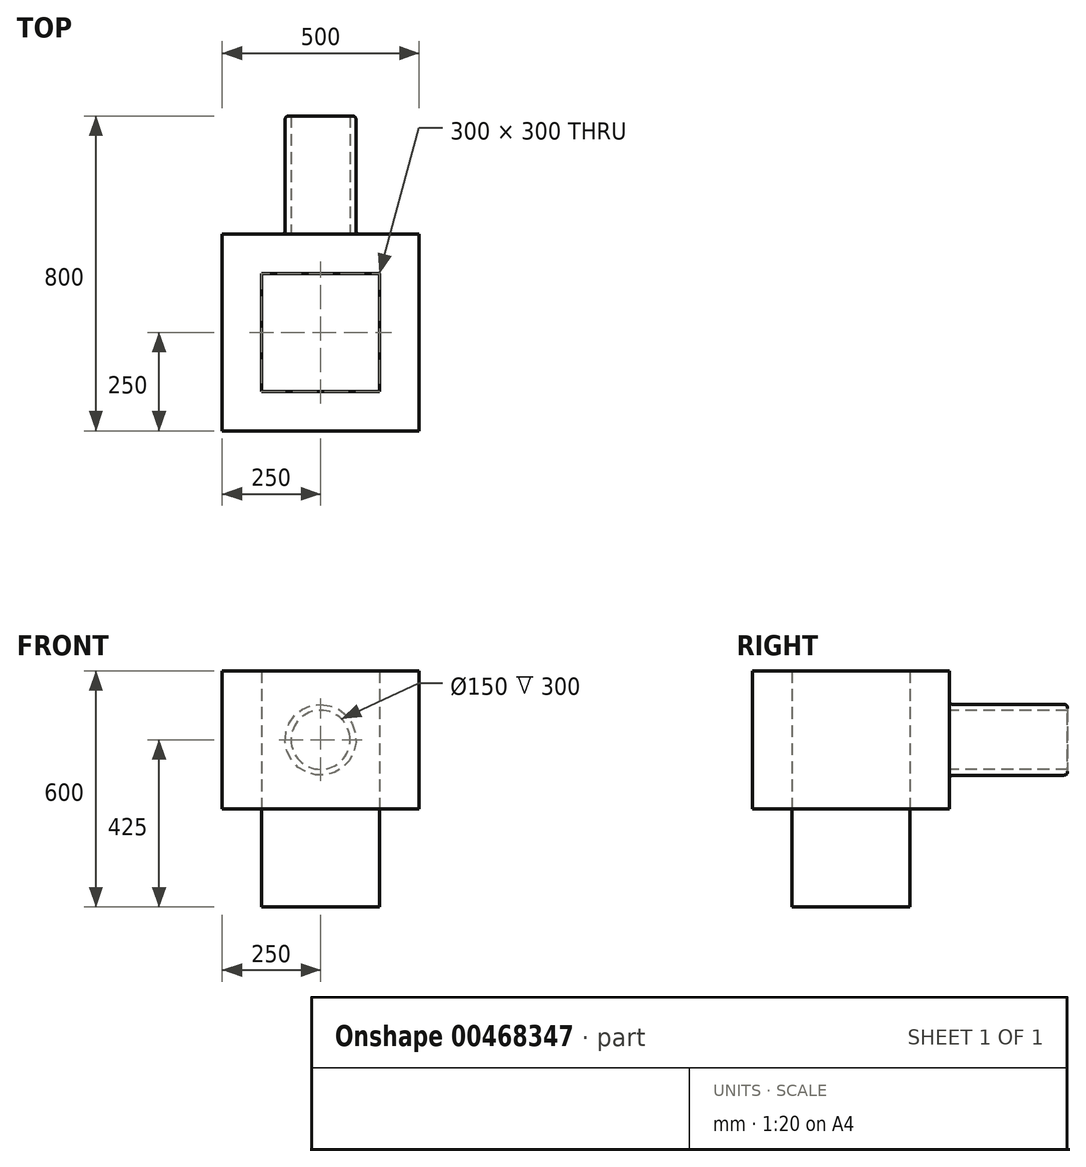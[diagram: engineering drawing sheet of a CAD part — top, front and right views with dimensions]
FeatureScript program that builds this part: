
annotation { "Feature Type Name" : "Feature", "Feature Type Description" : "" }
export const myFeature = defineFeature(function(context is Context, id is Id, definition is map)
    precondition{}
    {
        {
            var Q0;
            Q0=qCreatedBy(makeId("Top.planeOp"),FACE);
            var sketch = newSketch(context, id + "F0", { "sketchPlane" : qUnion([Q0])});
            skLineSegment(sketch, "E0", {"start": v(0, 0) * mm, "end": v(0, 500) * mm});
            skLineSegment(sketch, "E1", {"start": v(0, 500) * mm, "end": v(500, 500) * mm});
            skLineSegment(sketch, "E2", {"start": v(500, 500) * mm, "end": v(500, 0) * mm});
            skLineSegment(sketch, "E3", {"start": v(500, 0) * mm, "end": v(0, 0) * mm});
            skLineSegment(sketch, "E4.0", {"start": v(100, 100) * mm, "end": v(100, 400) * mm});
            skLineSegment(sketch, "E5.0", {"start": v(100, 400) * mm, "end": v(400, 400) * mm});
            skLineSegment(sketch, "E6.0", {"start": v(400, 100) * mm, "end": v(100, 100) * mm});
            skLineSegment(sketch, "E7.0", {"start": v(400, 400) * mm, "end": v(400, 100) * mm});
            skSolve(sketch);
        }
        {
            var Q0;
            Q0=makeQuery(id+"F0.imprint","IMPRINT",FACE,{"disambiguationData":[TD([[makeQuery(id+"F0.imprint","IMPRINT",EDGE,{"derivedFrom":sQuery(id+"F0.wireOp",EDGE,"E0")}),-1.0]])]});
            extrude(context, id + "F1", {"entities" : qUnion([Q0]), "depth" : 350 * mm, "offsetDistance" : 25 * mm});
        }
        {
            var Q0;
            Q0=makeQuery(id+"F1.opExtrude","CAP_FACE",FACE,{"disambiguationData":[OSD([sQuery(id+"F0.wireOp",EDGE,"E0"),sQuery(id+"F0.wireOp",EDGE,"E1"),sQuery(id+"F0.wireOp",EDGE,"E2"),sQuery(id+"F0.wireOp",EDGE,"E3"),sQuery(id+"F0.wireOp",EDGE,"E4.0"),sQuery(id+"F0.wireOp",EDGE,"E5.0"),sQuery(id+"F0.wireOp",EDGE,"E6.0"),sQuery(id+"F0.wireOp",EDGE,"E7.0")])],"isStart":true});
            var sketch = newSketch(context, id + "F2", { "sketchPlane" : qUnion([Q0])});
            skLineSegment(sketch, "E8.bottom", {"start": v(400, -100) * mm, "end": v(100, -100) * mm});
            skLineSegment(sketch, "E8.top", {"start": v(400, -400) * mm, "end": v(100, -400) * mm});
            skLineSegment(sketch, "E8.left", {"start": v(400, -100) * mm, "end": v(400, -400) * mm});
            skLineSegment(sketch, "E8.right", {"start": v(100, -100) * mm, "end": v(100, -400) * mm});
            skSolve(sketch);
        }
        {
            var Q0;
            Q0 = qSketchRegion(id + "F2", true);
            extrude(context, id + "F3", {"entities" : qUnion([Q0]), "depth" : 250 * mm, "offsetDistance" : 25 * mm});
        }
        {
            var Q0;
            Q0=makeQuery(id+"F1.opExtrude","SWEPT_FACE",FACE,{"disambiguationData":[OSD([sQuery(id+"F0.wireOp",EDGE,"E1")])]});
            var sketch = newSketch(context, id + "F4", { "sketchPlane" : qUnion([Q0])});
            skCircle(sketch, "E9", {"center": v(-250, 175) * mm, "radius": 75 * mm});
            skLineSegment(sketch, "E10", {"start": v(-250, 175) * mm, "end": v(-250, 0) * mm, "construction": true});
            skLineSegment(sketch, "E11", {"start": v(-250, 175) * mm, "end": v(0, 175) * mm, "construction": true});
            skCircle(sketch, "E12.0", {"center": v(-250, 175) * mm, "radius": 90 * mm});
            skSolve(sketch);
        }
        {
            var Q0;
            Q0 = qSketchRegion(id + "F4", true);
            extrude(context, id + "F5", {"entities" : qUnion([Q0]), "operationType" : NewBodyOperationType.ADD, "depth" : 300 * mm, "offsetDistance" : 25 * mm});
        }
        {
            var Q0;
            Q0=makeQuery(id+"F5.opExtrude","SWEPT_FACE",FACE,{"disambiguationData":[OSD([sQuery(id+"F4.wireOp",EDGE,"E12.0")])]});
            fillet(context, id + "F6", {"entities" : qUnion([Q0]), "radius" : 10 * mm, "tangentPropagation" : true, "rho" : 0.5, "crossSection" : FilletCrossSection.CONIC, "allowEdgeOverflow" : false});
        }
    });
